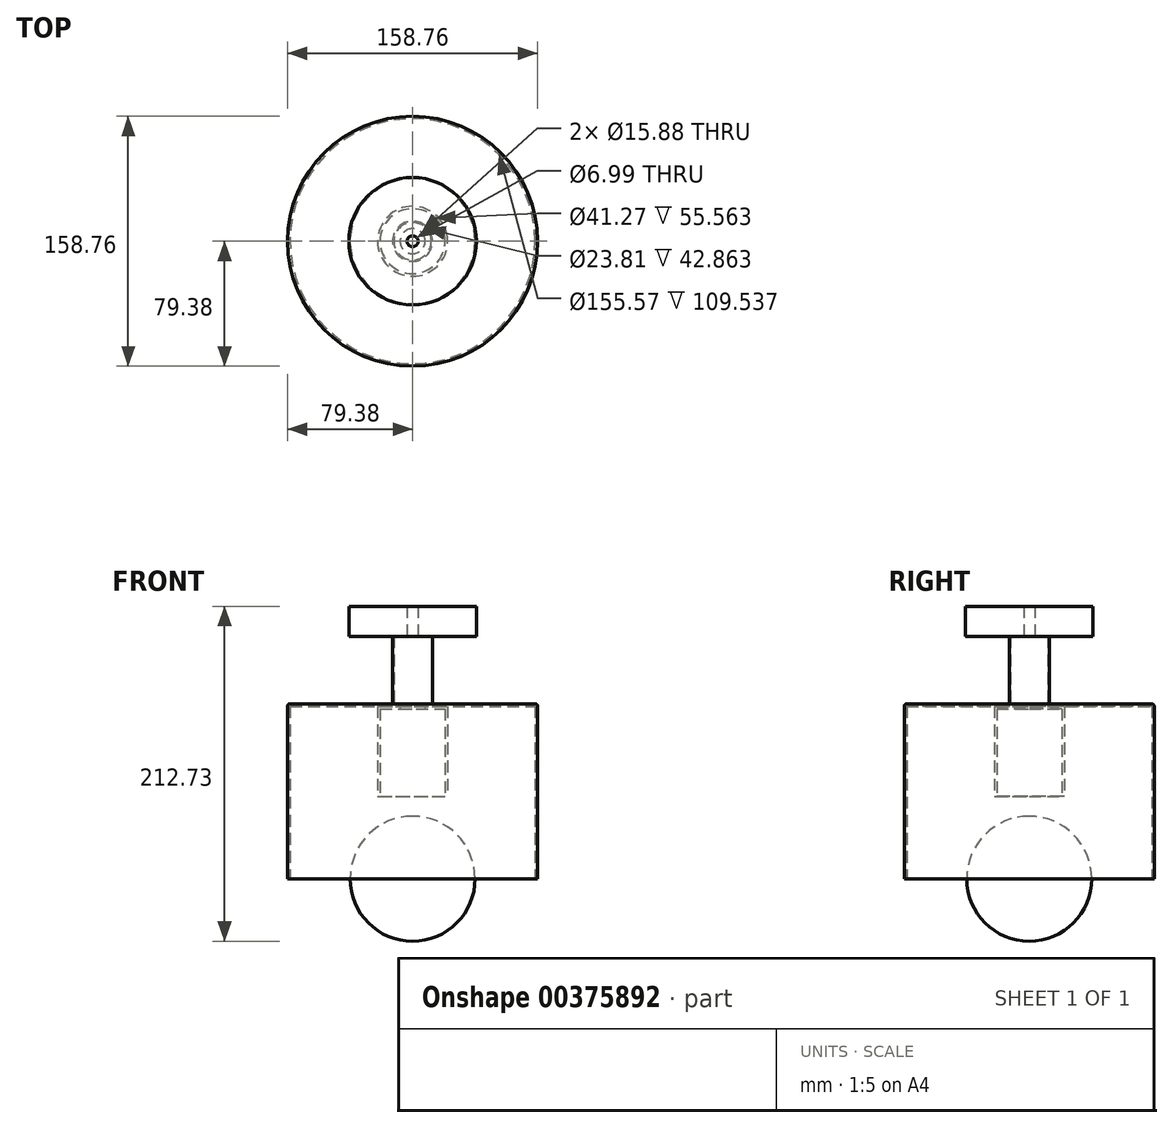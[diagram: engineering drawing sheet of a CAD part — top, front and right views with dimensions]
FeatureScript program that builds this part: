
annotation { "Feature Type Name" : "Feature", "Feature Type Description" : "" }
export const myFeature = defineFeature(function(context is Context, id is Id, definition is map)
    precondition{}
    {
        {
            var Q0;
            Q0=qCreatedBy(makeId("Front.planeOp"),FACE);
            var sketch = newSketch(context, id + "F0", { "sketchPlane" : qUnion([Q0])});
            skLineSegment(sketch, "E0", {"start": v(-77.79, 0) * mm, "end": v(-77.79, 109.54) * mm});
            skLineSegment(sketch, "E1", {"start": v(-77.79, 109.54) * mm, "end": v(-7.94, 109.54) * mm});
            skLineSegment(sketch, "E2", {"start": v(-7.94, 109.54) * mm, "end": v(-7.94, 111.13) * mm});
            skLineSegment(sketch, "E3", {"start": v(-7.94, 111.12) * mm, "end": v(-79.38, 111.12) * mm});
            skLineSegment(sketch, "E4", {"start": v(-79.38, 111.12) * mm, "end": v(-79.38, 0) * mm});
            skLineSegment(sketch, "E5", {"start": v(-79.38, 0) * mm, "end": v(-77.79, 0) * mm});
            skLineSegment(sketch, "E6", {"start": v(-12.7, 153.99) * mm, "end": v(-12.7, 111.13) * mm});
            skLineSegment(sketch, "E7", {"start": v(-11.9, 111.13) * mm, "end": v(-11.9, 153.99) * mm});
            skLineSegment(sketch, "E8", {"start": v(-11.9, 153.99) * mm, "end": v(-12.7, 153.99) * mm});
            skLineSegment(sketch, "E9", {"start": v(-20.64, 107.95) * mm, "end": v(-20.64, 52.39) * mm});
            skLineSegment(sketch, "E10", {"start": v(-22.23, 52.39) * mm, "end": v(-20.64, 52.39) * mm});
            skLineSegment(sketch, "E11", {"start": v(-22.23, 52.39) * mm, "end": v(-22.23, 109.54) * mm});
            skLineSegment(sketch, "E12", {"start": v(0, 0) * mm, "end": v(0, 122.02) * mm, "construction": true});
            skCircle(sketch, "E13", {"center": v(0, 0) * mm, "radius": 39.69 * mm});
            skLineSegment(sketch, "E14", {"start": v(0, 39.69) * mm, "end": v(0, -39.69) * mm});
            skLineSegment(sketch, "E15", {"start": v(-20.64, 107.95) * mm, "end": v(-7.94, 107.95) * mm});
            skLineSegment(sketch, "E16", {"start": v(-7.94, 107.95) * mm, "end": v(-7.94, 109.54) * mm});
            skLineSegment(sketch, "E17.bottom", {"start": v(-40.48, 173.04) * mm, "end": v(-3.5, 173.04) * mm});
            skLineSegment(sketch, "E17.top", {"start": v(-40.48, 153.99) * mm, "end": v(-3.5, 153.99) * mm});
            skLineSegment(sketch, "E17.left", {"start": v(-40.48, 173.04) * mm, "end": v(-40.48, 153.99) * mm});
            skLineSegment(sketch, "E17.right", {"start": v(-3.5, 173.04) * mm, "end": v(-3.5, 153.99) * mm});
            skSolve(sketch);
        }
        {
            var Q0;
            {var subQ0=sQuery(id+"F0.wireOp",EDGE,"E14");Q0=makeQuery(id+"F0.imprint","IMPRINT",FACE,{"disambiguationData":[TD([[makeQuery(id+"F0.imprint","IMPRINT",EDGE,{"derivedFrom":subQ0}),-1.0]])]});}
            var Q1;
            Q1=sQuery(id+"F0.wireOp",EDGE,"E14");
            revolve(context, id + "F1", {"entities" : qUnion([Q0]), "axis" : qUnion([Q1]), "revolveType" : RevolveType.FULL});
        }
        {
            var Q0;
            {var subQ4=sQuery(id+"F0.wireOp",EDGE,"E0");Q0=makeQuery(id+"F0.imprint","IMPRINT",FACE,{"disambiguationData":[TD([[makeQuery(id+"F0.imprint","IMPRINT",EDGE,{"derivedFrom":subQ4}),1.0]])]});}
            var Q1;
            Q1=sQuery(id+"F0.wireOp",EDGE,"E12");
            revolve(context, id + "F2", {"entities" : qUnion([Q0]), "axis" : qUnion([Q1]), "revolveType" : RevolveType.FULL});
        }
        {
            var Q0;
            Q0=makeQuery(id+"F2.opRevolve","SWEPT_EDGE",EDGE,{"disambiguationData":[OSD([sQuery(id+"F0.wireOp",EDGE,"E3"),sQuery(id+"F0.wireOp",EDGE,"E4")])]});
            fillet(context, id + "F3", {"entities" : qUnion([Q0]), "radius" : 1.59 * mm, "tangentPropagation" : true, "allowEdgeOverflow" : false});
        }
        {
            var Q0;
            {var subQ0=sQuery(id+"F0.wireOp",EDGE,"E9");Q0=makeQuery(id+"F0.imprint","IMPRINT",FACE,{"disambiguationData":[TD([[makeQuery(id+"F0.imprint","IMPRINT",EDGE,{"derivedFrom":subQ0}),-1.0]])]});}
            var Q1;
            Q1=sQuery(id+"F0.wireOp",EDGE,"E12");
            revolve(context, id + "F4", {"entities" : qUnion([Q0]), "axis" : qUnion([Q1]), "revolveType" : RevolveType.FULL});
        }
        {
            var Q0;
            {var subQ0=sQuery(id+"F0.wireOp",EDGE,"E6");Q0=makeQuery(id+"F0.imprint","IMPRINT",FACE,{"disambiguationData":[TD([[makeQuery(id+"F0.imprint","IMPRINT",EDGE,{"derivedFrom":subQ0}),1.0]])]});}
            var Q1;
            Q1=sQuery(id+"F0.wireOp",EDGE,"E12");
            revolve(context, id + "F5", {"entities" : qUnion([Q0]), "axis" : qUnion([Q1]), "revolveType" : RevolveType.FULL});
        }
        {
            var Q0;
            Q0=makeQuery(id+"F0.imprint","IMPRINT",FACE,{"disambiguationData":[TD([[makeQuery(id+"F0.imprint","IMPRINT",EDGE,{"derivedFrom":sQuery(id+"F0.wireOp",EDGE,"E17.bottom")}),-1.0]])]});
            var Q1;
            Q1=sQuery(id+"F0.wireOp",EDGE,"E12");
            revolve(context, id + "F6", {"entities" : qUnion([Q0]), "axis" : qUnion([Q1]), "revolveType" : RevolveType.FULL});
        }
    });
